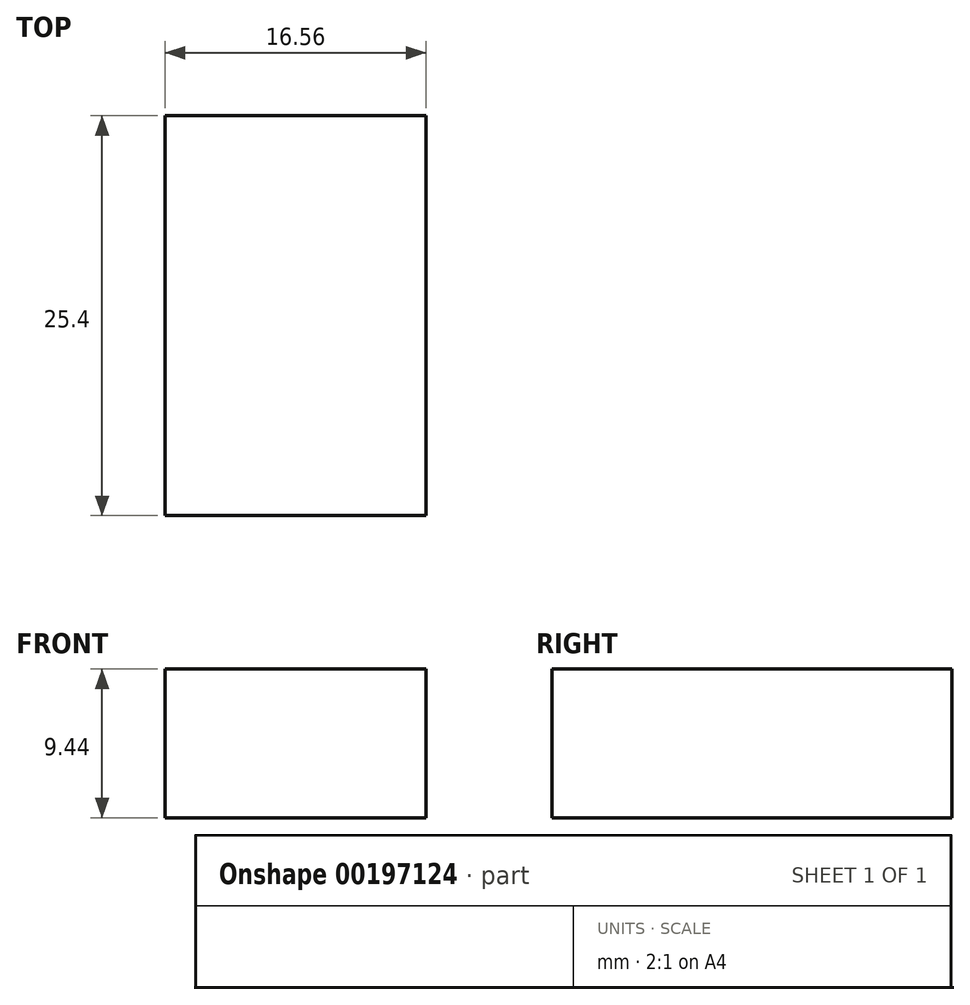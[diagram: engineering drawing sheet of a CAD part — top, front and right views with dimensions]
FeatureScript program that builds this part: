
annotation { "Feature Type Name" : "Feature", "Feature Type Description" : "" }
export const myFeature = defineFeature(function(context is Context, id is Id, definition is map)
    precondition{}
    {
        {
            var Q0;
            Q0=qCreatedBy(makeId("Front.planeOp"),FACE);
            var sketch = newSketch(context, id + "F0", { "sketchPlane" : qUnion([Q0])});
            skLineSegment(sketch, "E0.bottom", {"start": v(-99.07, 40.71) * mm, "end": v(-82.51, 40.71) * mm});
            skLineSegment(sketch, "E0.top", {"start": v(-99.07, 31.27) * mm, "end": v(-82.51, 31.27) * mm});
            skLineSegment(sketch, "E0.left", {"start": v(-99.07, 40.71) * mm, "end": v(-99.07, 31.27) * mm});
            skLineSegment(sketch, "E0.right", {"start": v(-82.51, 40.71) * mm, "end": v(-82.51, 31.27) * mm});
            skSolve(sketch);
        }
        {
            var Q0;
            Q0 = qSketchRegion(id + "F0", true);
            extrude(context, id + "F1", {"entities" : qUnion([Q0]), "depth" : 25.4 * mm});
        }
    });
